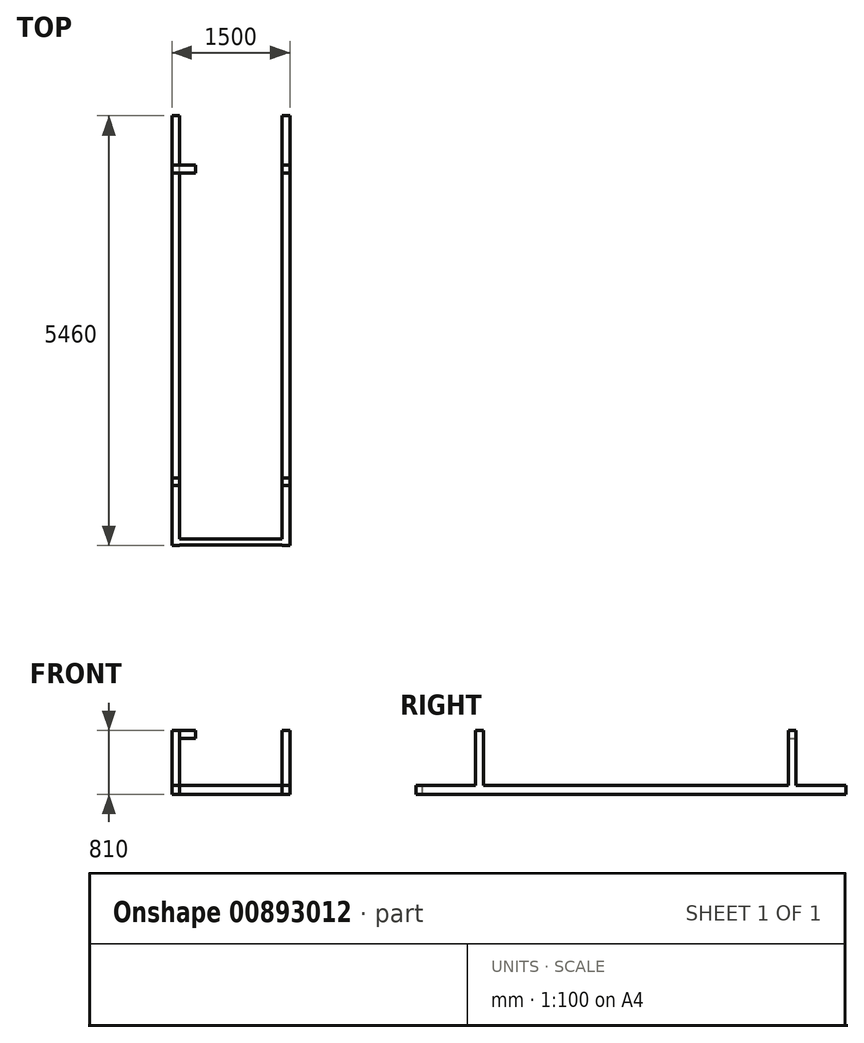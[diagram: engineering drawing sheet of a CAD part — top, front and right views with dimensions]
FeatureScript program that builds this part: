
annotation { "Feature Type Name" : "Feature", "Feature Type Description" : "" }
export const myFeature = defineFeature(function(context is Context, id is Id, definition is map)
    precondition{}
    {
        {
            var Q0;
            Q0=qCreatedBy(makeId("Top.planeOp"),FACE);
            var sketch = newSketch(context, id + "F0", { "sketchPlane" : qUnion([Q0])});
            skLineSegment(sketch, "E0.bottom", {"start": v(750, -2850) * mm, "end": v(650, -2850) * mm});
            skLineSegment(sketch, "E0.top", {"start": v(750, 2850) * mm, "end": v(650, 2850) * mm});
            skLineSegment(sketch, "E0.left", {"start": v(750, -2850) * mm, "end": v(750, 2850) * mm});
            skLineSegment(sketch, "E0.right", {"start": v(-750, -2850) * mm, "end": v(-750, 2850) * mm});
            skPoint(sketch, "E0.middle", {"position": v(0, 0) * mm});
            skLineSegment(sketch, "E1.left", {"start": v(-650, 2850) * mm, "end": v(-650, -2850) * mm});
            skLineSegment(sketch, "E1.right", {"start": v(650, 2850) * mm, "end": v(650, -2850) * mm});
            skLineSegment(sketch, "E2.trimOffspring", {"start": v(-650, 2850) * mm, "end": v(-750, 2850) * mm});
            skLineSegment(sketch, "E3.trimOffspring", {"start": v(-650, -2850) * mm, "end": v(-750, -2850) * mm});
            skSolve(sketch);
        }
        {
            var Q0;
            Q0=qSketchRegion(id+"F0",true);
            extrude(context, id + "F1", {"entities" : qUnion([Q0]), "depth" : 110 * mm, "offsetDistance" : 25 * mm});
        }
        {
            var Q0;
            Q0=makeQuery(id+"F1.opExtrude","SWEPT_FACE",FACE,{"disambiguationData":[OSD([sQuery(id+"F0.wireOp",EDGE,"E1.left")])]});
            var sketch = newSketch(context, id + "F2", { "sketchPlane" : qUnion([Q0])});
            skLineSegment(sketch, "E4.bottom", {"start": v(-2604.7, 110) * mm, "end": v(-2524.7, 110) * mm});
            skLineSegment(sketch, "E4.top", {"start": v(-2604.7, 0) * mm, "end": v(-2524.7, 0) * mm});
            skLineSegment(sketch, "E4.left", {"start": v(-2604.7, 110) * mm, "end": v(-2604.7, 0) * mm});
            skLineSegment(sketch, "E4.right", {"start": v(-2524.7, 110) * mm, "end": v(-2524.7, 0) * mm});
            skSolve(sketch);
        }
        {
            var Q0;
            Q0=makeQuery(id+"F2.imprint","IMPRINT",FACE,{"disambiguationData":[TD([[makeQuery(id+"F2.imprint","IMPRINT",EDGE,{"derivedFrom":sQuery(id+"F2.wireOp",EDGE,"E4.bottom")}),1.0]])]});
            extrude(context, id + "F3", {"entities" : qUnion([Q0]), "operationType" : NewBodyOperationType.ADD, "depth" : 1350 * mm, "offsetDistance" : 25 * mm});
        }
        {
            var Q0;
            Q0=makeQuery(id+"F3.boolean.opBoolean","MERGE",FACE,{"derivedFrom":[makeQuery(id+"F1.opExtrude","CAP_FACE",FACE,{"disambiguationData":[OSD([sQuery(id+"F0.wireOp",EDGE,"E0.bottom"),sQuery(id+"F0.wireOp",EDGE,"E0.top"),sQuery(id+"F0.wireOp",EDGE,"E0.left"),sQuery(id+"F0.wireOp",EDGE,"E1.right")])],"isStart":false}),makeQuery(id+"F1.opExtrude","CAP_FACE",FACE,{"disambiguationData":[OSD([sQuery(id+"F0.wireOp",EDGE,"E0.right"),sQuery(id+"F0.wireOp",EDGE,"E1.left"),sQuery(id+"F0.wireOp",EDGE,"E2.trimOffspring"),sQuery(id+"F0.wireOp",EDGE,"E3.trimOffspring")])],"isStart":false}),makeQuery(id+"F3.opExtrude","SWEPT_FACE",FACE,{"disambiguationData":[OSD([sQuery(id+"F2.wireOp",EDGE,"E4.bottom")])]})]});
            var sketch = newSketch(context, id + "F4", { "sketchPlane" : qUnion([Q0])});
            skLineSegment(sketch, "E5.bottom", {"start": v(650, -1850) * mm, "end": v(750, -1850) * mm});
            skLineSegment(sketch, "E5.top", {"start": v(650, -1750) * mm, "end": v(750, -1750) * mm});
            skLineSegment(sketch, "E5.left", {"start": v(650, -1850) * mm, "end": v(650, -1750) * mm});
            skLineSegment(sketch, "E5.right", {"start": v(750, -1850) * mm, "end": v(750, -1750) * mm});
            skLineSegment(sketch, "E6.0.1.0", {"start": v(750, 2120) * mm, "end": v(750, 2220) * mm});
            skLineSegment(sketch, "E6.0.1.1", {"start": v(650, 2120) * mm, "end": v(650, 2220) * mm});
            skLineSegment(sketch, "E6.0.1.2", {"start": v(650, 2220) * mm, "end": v(750, 2220) * mm});
            skLineSegment(sketch, "E6.0.1.3", {"start": v(650, 2120) * mm, "end": v(750, 2120) * mm});
            skLineSegment(sketch, "E6.1.0.0", {"start": v(-650, -1850) * mm, "end": v(-650, -1750) * mm});
            skLineSegment(sketch, "E6.1.0.1", {"start": v(-750, -1850) * mm, "end": v(-750, -1750) * mm});
            skLineSegment(sketch, "E6.1.0.2", {"start": v(-750, -1750) * mm, "end": v(-650, -1750) * mm});
            skLineSegment(sketch, "E6.1.0.3", {"start": v(-750, -1850) * mm, "end": v(-650, -1850) * mm});
            skLineSegment(sketch, "E6.1.1.0", {"start": v(-650, 2120) * mm, "end": v(-650, 2220) * mm});
            skLineSegment(sketch, "E6.1.1.1", {"start": v(-750, 2120) * mm, "end": v(-750, 2220) * mm});
            skLineSegment(sketch, "E6.1.1.2", {"start": v(-750, 2220) * mm, "end": v(-650, 2220) * mm});
            skLineSegment(sketch, "E6.1.1.3", {"start": v(-750, 2120) * mm, "end": v(-650, 2120) * mm});
            skLineSegment(sketch, "E6.direction1", {"start": v(650, -1850) * mm, "end": v(-750, -1850) * mm, "construction": true});
            skLineSegment(sketch, "E6.direction2", {"start": v(650, -1850) * mm, "end": v(650, 2120) * mm, "construction": true});
            skSolve(sketch);
        }
        {
            var Q0;
            Q0=qSketchRegion(id+"F4",true);
            extrude(context, id + "F5", {"entities" : qUnion([Q0]), "operationType" : NewBodyOperationType.ADD, "depth" : 700 * mm, "offsetDistance" : 25 * mm});
        }
        {
            var Q0;
            Q0=makeQuery(id+"F1.opExtrude","SWEPT_FACE",FACE,{"disambiguationData":[OSD([sQuery(id+"F0.wireOp",EDGE,"E0.bottom")])]});
            var Q1;
            Q1=makeQuery(id+"F1.opExtrude","SWEPT_FACE",FACE,{"disambiguationData":[OSD([sQuery(id+"F0.wireOp",EDGE,"E3.trimOffspring")])]});
            extrude(context, id + "F6", {"entities" : qUnion([Q0, Q1]), "operationType" : NewBodyOperationType.REMOVE, "oppositeDirection" : true, "depth" : 240 * mm, "offsetDistance" : 25 * mm});
        }
        {
            var Q0;
            {var subQ1=sQuery(id+"F0.wireOp",EDGE,"E2.trimOffspring");var subQ2=sQuery(id+"F0.wireOp",EDGE,"E1.left");Q0=makeQuery(id+"F5.boolean.opBoolean","MERGE",FACE,{"derivedFrom":[makeQuery(id+"F3.boolean.opBoolean","SPLIT",FACE,{"disambiguationData":[TD([makeQuery(id+"F1.opExtrude","SWEPT_FACE",FACE,{"disambiguationData":[OSD([subQ1])]})])],"derivedFrom":makeQuery(id+"F1.opExtrude","SWEPT_FACE",FACE,{"disambiguationData":[OSD([subQ2])]})}),makeQuery(id+"F5.opExtrude","SWEPT_FACE",FACE,{"disambiguationData":[OSD([sQuery(id+"F4.wireOp",EDGE,"E6.1.0.0")])]}),makeQuery(id+"F5.opExtrude","SWEPT_FACE",FACE,{"disambiguationData":[OSD([sQuery(id+"F4.wireOp",EDGE,"E6.1.1.0")])]})]});}
            var sketch = newSketch(context, id + "F7", { "sketchPlane" : qUnion([Q0])});
            skLineSegment(sketch, "E7.bottom", {"start": v(2120, 810) * mm, "end": v(2220, 810) * mm});
            skLineSegment(sketch, "E7.top", {"start": v(2120, 710) * mm, "end": v(2220, 710) * mm});
            skLineSegment(sketch, "E7.left", {"start": v(2120, 810) * mm, "end": v(2120, 710) * mm});
            skLineSegment(sketch, "E7.right", {"start": v(2220, 810) * mm, "end": v(2220, 710) * mm});
            skSolve(sketch);
        }
        {
            var Q0;
            Q0=makeQuery(id+"F7.imprint","IMPRINT",FACE,{"disambiguationData":[TD([[makeQuery(id+"F7.imprint","IMPRINT",EDGE,{"derivedFrom":sQuery(id+"F7.wireOp",EDGE,"E7.bottom")}),1.0]])]});
            extrude(context, id + "F8", {"entities" : qUnion([Q0]), "operationType" : NewBodyOperationType.ADD, "depth" : 200 * mm, "offsetDistance" : 25 * mm});
        }
    });
